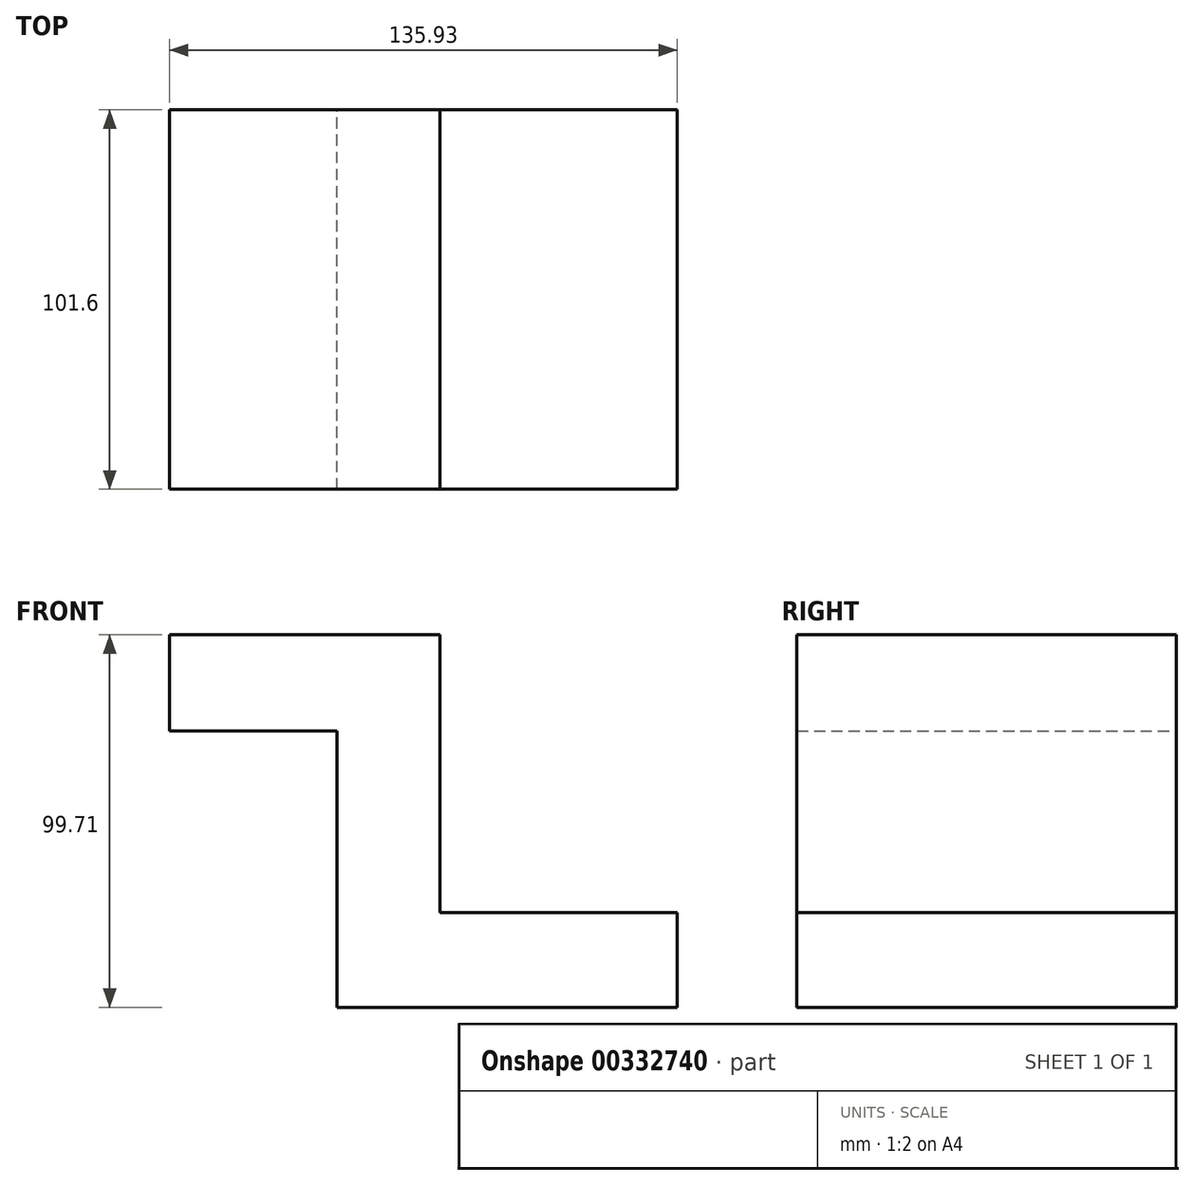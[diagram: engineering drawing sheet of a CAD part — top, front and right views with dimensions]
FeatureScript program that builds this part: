
annotation { "Feature Type Name" : "Feature", "Feature Type Description" : "" }
export const myFeature = defineFeature(function(context is Context, id is Id, definition is map)
    precondition{}
    {
        {
            var Q0;
            Q0=qCreatedBy(makeId("Front.planeOp"),FACE);
            var sketch = newSketch(context, id + "F0", { "sketchPlane" : qUnion([Q0])});
            skLineSegment(sketch, "E0", {"start": v(-67.15, 49.7) * mm, "end": v(5.28, 49.7) * mm});
            skLineSegment(sketch, "E1", {"start": v(5.28, 49.7) * mm, "end": v(5.28, -24.61) * mm});
            skLineSegment(sketch, "E2", {"start": v(5.28, -24.61) * mm, "end": v(68.78, -24.61) * mm});
            skLineSegment(sketch, "E3", {"start": v(68.78, -24.61) * mm, "end": v(68.78, -50.01) * mm});
            skLineSegment(sketch, "E4", {"start": v(68.78, -50.01) * mm, "end": v(-22.31, -50.01) * mm});
            skLineSegment(sketch, "E5", {"start": v(-22.31, -50.01) * mm, "end": v(-22.31, 24) * mm});
            skLineSegment(sketch, "E6", {"start": v(-22.31, 24) * mm, "end": v(-67.15, 24) * mm});
            skLineSegment(sketch, "E7", {"start": v(-67.15, 24) * mm, "end": v(-67.15, 49.7) * mm});
            skSolve(sketch);
        }
        {
            var Q0;
            Q0=makeQuery(id+"F0.imprint","IMPRINT",FACE,{"disambiguationData":[TD([[makeQuery(id+"F0.imprint","IMPRINT",EDGE,{"derivedFrom":sQuery(id+"F0.wireOp",EDGE,"E0")}),-1.0]])]});
            extrude(context, id + "F1", {"entities" : qUnion([Q0]), "depth" : 25.4 * mm});
        }
        {
            var Q0;
            Q0=makeQuery(id+"F1.opExtrude","CAP_FACE",FACE,{"disambiguationData":[OSD([sQuery(id+"F0.wireOp",EDGE,"E0"),sQuery(id+"F0.wireOp",EDGE,"E1"),sQuery(id+"F0.wireOp",EDGE,"E2"),sQuery(id+"F0.wireOp",EDGE,"E3"),sQuery(id+"F0.wireOp",EDGE,"E4"),sQuery(id+"F0.wireOp",EDGE,"E5"),sQuery(id+"F0.wireOp",EDGE,"E6"),sQuery(id+"F0.wireOp",EDGE,"E7")])],"isStart":false});
            extrude(context, id + "F2", {"entities" : qUnion([Q0]), "operationType" : NewBodyOperationType.ADD, "depth" : 76.2 * mm});
        }
    });
